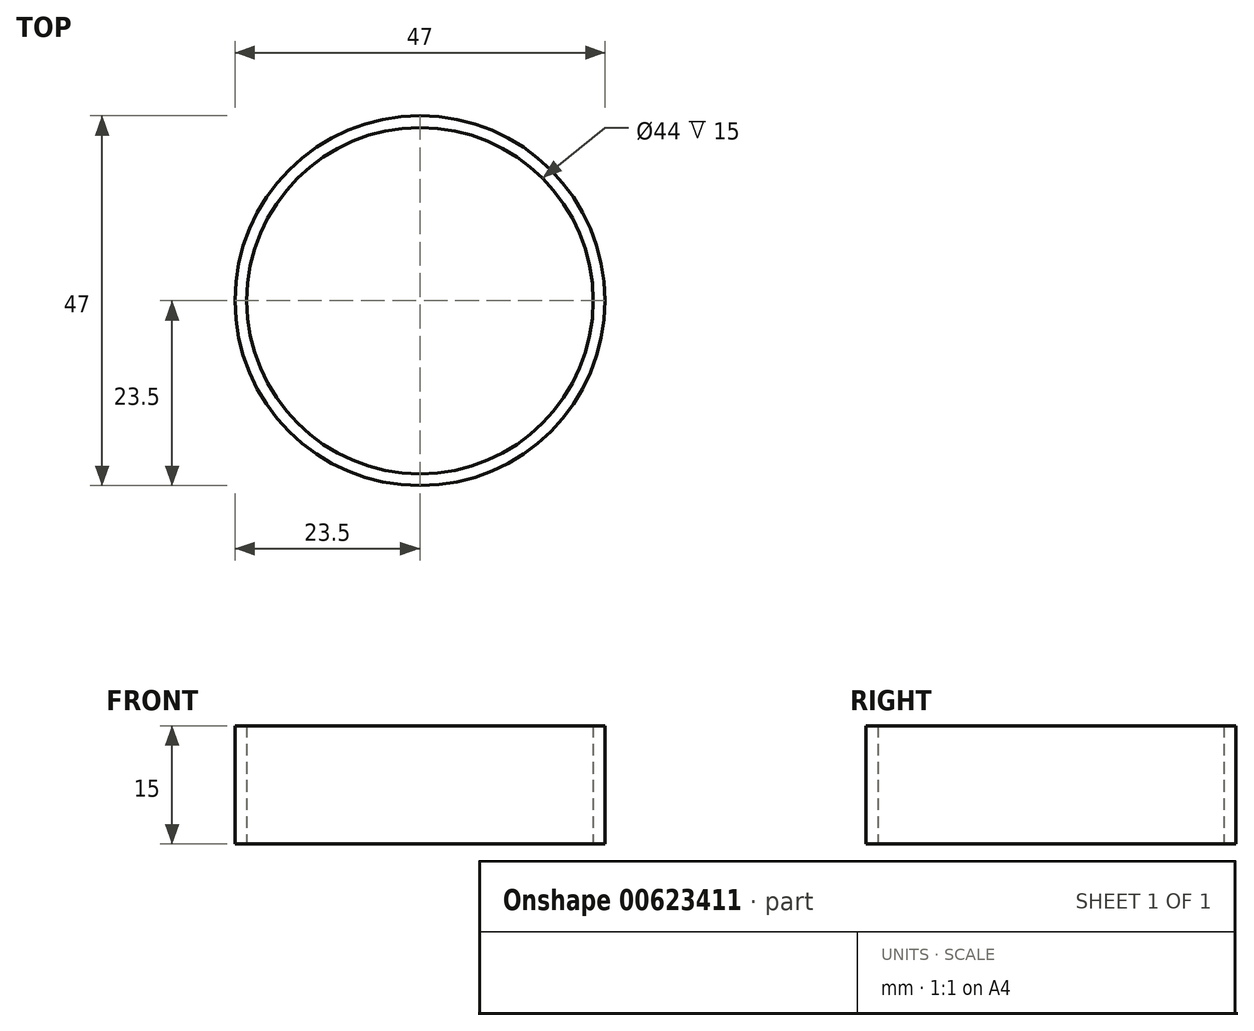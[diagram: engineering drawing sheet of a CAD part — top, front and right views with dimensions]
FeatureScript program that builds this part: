
annotation { "Feature Type Name" : "Feature", "Feature Type Description" : "" }
export const myFeature = defineFeature(function(context is Context, id is Id, definition is map)
    precondition{}
    {
        {
            var Q0;
            Q0=qCreatedBy(makeId("Top.planeOp"),FACE);
            var sketch = newSketch(context, id + "F0", { "sketchPlane" : qUnion([Q0])});
            skCircle(sketch, "E0", {"center": v(0, 0) * mm, "radius": 22 * mm});
            skCircle(sketch, "E1.0", {"center": v(0, 0) * mm, "radius": 23.5 * mm});
            skSolve(sketch);
        }
        {
            var Q0;
            Q0=makeQuery(id+"F0.imprint","IMPRINT",FACE,{"disambiguationData":[TD([[makeQuery(id+"F0.imprint","IMPRINT",EDGE,{"derivedFrom":sQuery(id+"F0.wireOp",EDGE,"E0")}),-1.0]])]});
            extrude(context, id + "F1", {"entities" : qUnion([Q0]), "depth" : 15 * mm, "offsetDistance" : 25 * mm});
        }
    });
